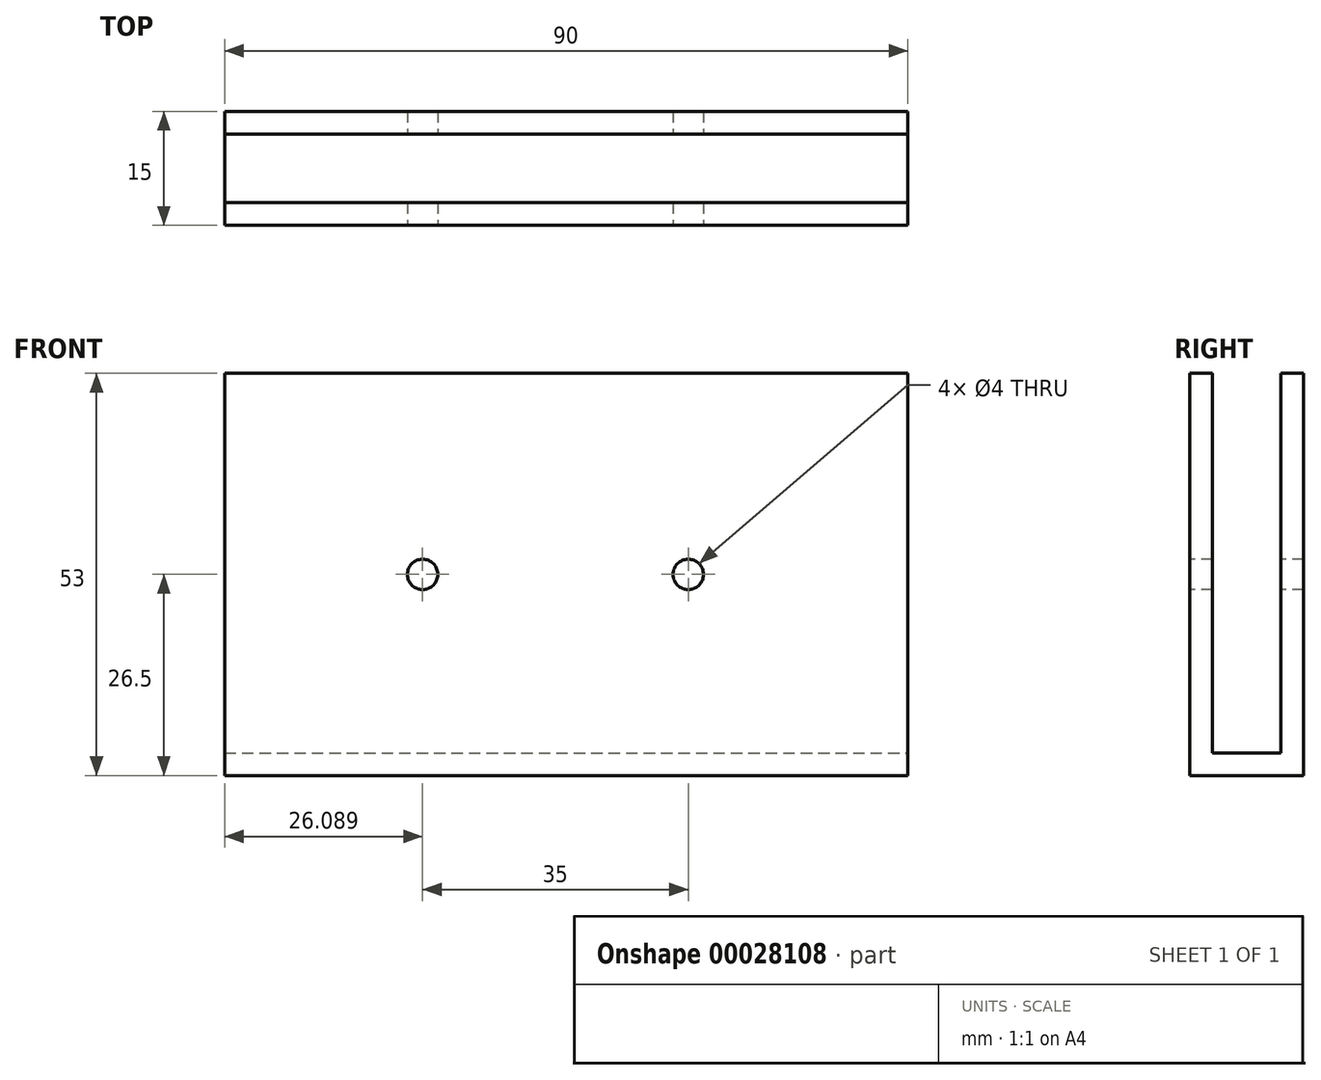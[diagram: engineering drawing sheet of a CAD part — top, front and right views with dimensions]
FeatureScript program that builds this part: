
annotation { "Feature Type Name" : "Feature", "Feature Type Description" : "" }
export const myFeature = defineFeature(function(context is Context, id is Id, definition is map)
    precondition{}
    {
        {
            var Q0;
            Q0=qCreatedBy(makeId("Top.planeOp"),FACE);
            var sketch = newSketch(context, id + "F0", { "sketchPlane" : qUnion([Q0])});
            skLineSegment(sketch, "E0.bottom", {"start": v(-4.29, 7.51) * mm, "end": v(85.71, 7.51) * mm});
            skLineSegment(sketch, "E0.top", {"start": v(-4.29, -7.49) * mm, "end": v(85.71, -7.49) * mm});
            skLineSegment(sketch, "E0.left", {"start": v(-4.29, 7.51) * mm, "end": v(-4.29, -7.49) * mm});
            skLineSegment(sketch, "E0.right", {"start": v(85.71, 7.51) * mm, "end": v(85.71, -7.49) * mm});
            skSolve(sketch);
        }
        {
            var Q0;
            Q0=qSketchRegion(id+"F0",true);
            extrude(context, id + "F1", {"entities" : qUnion([Q0]), "depth" : 3 * mm});
        }
        {
            var Q0;
            Q0=makeQuery(id+"F1.opExtrude","CAP_FACE",FACE,{"disambiguationData":[OSD([sQuery(id+"F0.wireOp",EDGE,"E0.bottom"),sQuery(id+"F0.wireOp",EDGE,"E0.top"),sQuery(id+"F0.wireOp",EDGE,"E0.left"),sQuery(id+"F0.wireOp",EDGE,"E0.right")])],"isStart":false});
            var sketch = newSketch(context, id + "F2", { "sketchPlane" : qUnion([Q0])});
            skLineSegment(sketch, "E1.bottom", {"start": v(-4.29, 7.51) * mm, "end": v(85.71, 7.51) * mm});
            skLineSegment(sketch, "E1.top", {"start": v(-4.29, 4.51) * mm, "end": v(85.71, 4.51) * mm});
            skLineSegment(sketch, "E1.left", {"start": v(-4.29, 7.51) * mm, "end": v(-4.29, 4.51) * mm});
            skLineSegment(sketch, "E1.right", {"start": v(85.71, 7.51) * mm, "end": v(85.71, 4.51) * mm});
            skLineSegment(sketch, "E2.bottom", {"start": v(-4.29, -7.49) * mm, "end": v(85.71, -7.49) * mm});
            skLineSegment(sketch, "E2.top", {"start": v(-4.29, -4.49) * mm, "end": v(85.71, -4.49) * mm});
            skLineSegment(sketch, "E2.left", {"start": v(-4.29, -7.49) * mm, "end": v(-4.29, -4.49) * mm});
            skLineSegment(sketch, "E2.right", {"start": v(85.71, -7.49) * mm, "end": v(85.71, -4.49) * mm});
            skSolve(sketch);
        }
        {
            var Q0;
            Q0=qSketchRegion(id+"F2",true);
            extrude(context, id + "F3", {"entities" : qUnion([Q0]), "operationType" : NewBodyOperationType.ADD, "depth" : 50 * mm});
        }
        {
            var Q0;
            Q0=makeQuery(id+"F3.boolean.opBoolean","MERGE",FACE,{"derivedFrom":[makeQuery(id+"F1.opExtrude","SWEPT_FACE",FACE,{"disambiguationData":[OSD([sQuery(id+"F0.wireOp",EDGE,"E0.top")])]}),makeQuery(id+"F3.opExtrude","SWEPT_FACE",FACE,{"disambiguationData":[OSD([sQuery(id+"F2.wireOp",EDGE,"E2.bottom")])]})]});
            var sketch = newSketch(context, id + "F4", { "sketchPlane" : qUnion([Q0])});
            skPoint(sketch, "E3", {"position": v(85.71, 26.5) * mm});
            skPoint(sketch, "E4", {"position": v(56.8, 26.5) * mm});
            skPoint(sketch, "E5", {"position": v(21.8, 26.5) * mm});
            skCircle(sketch, "E6", {"center": v(21.8, 26.5) * mm, "radius": 2 * mm});
            skCircle(sketch, "E7", {"center": v(56.8, 26.5) * mm, "radius": 2 * mm});
            skSolve(sketch);
        }
        {
            var Q0;
            Q0=qSketchRegion(id+"F4",true);
            extrude(context, id + "F5", {"entities" : qUnion([Q0]), "operationType" : NewBodyOperationType.REMOVE, "endBound" : BoundingType.THROUGH_ALL, "oppositeDirection" : true, "depth" : 25 * mm});
        }
    });
